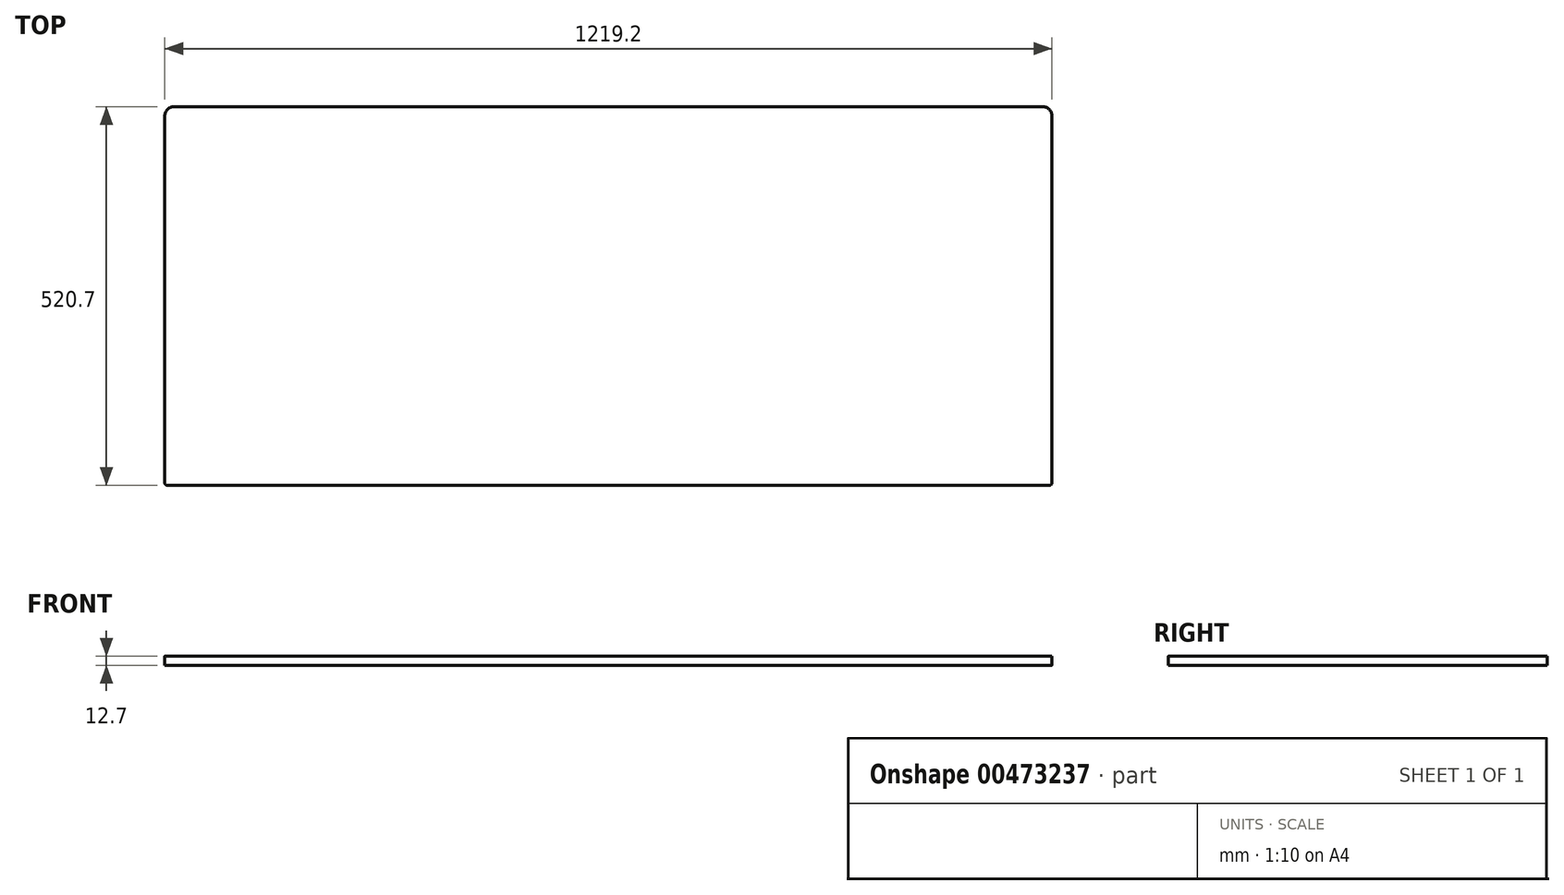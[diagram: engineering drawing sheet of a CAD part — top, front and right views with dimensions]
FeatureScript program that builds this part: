
annotation { "Feature Type Name" : "Feature", "Feature Type Description" : "" }
export const myFeature = defineFeature(function(context is Context, id is Id, definition is map)
    precondition{}
    {
        {
            var Q0;
            Q0=qCreatedBy(makeId("Top.planeOp"),FACE);
            var sketch = newSketch(context, id + "F0", { "sketchPlane" : qUnion([Q0])});
            skLineSegment(sketch, "E0.bottom", {"start": v(609.6, 260.35) * mm, "end": v(-609.6, 260.35) * mm});
            skLineSegment(sketch, "E0.top", {"start": v(609.6, -260.35) * mm, "end": v(-609.6, -260.35) * mm});
            skLineSegment(sketch, "E0.left", {"start": v(609.6, 260.35) * mm, "end": v(609.6, -260.35) * mm});
            skLineSegment(sketch, "E0.right", {"start": v(-609.6, 260.35) * mm, "end": v(-609.6, -260.35) * mm});
            skPoint(sketch, "E0.middle", {"position": v(0, 0) * mm});
            skSolve(sketch);
        }
        {
            var Q0;
            Q0=makeQuery(id+"F0.imprint","IMPRINT",FACE,{"disambiguationData":[TD([[makeQuery(id+"F0.imprint","IMPRINT",EDGE,{"derivedFrom":sQuery(id+"F0.wireOp",EDGE,"E0.bottom")}),1.0]])]});
            extrude(context, id + "F1", {"entities" : qUnion([Q0]), "depth" : 12.7 * mm});
        }
        {
            var Q0;
            Q0=makeQuery(id+"F1.opExtrude","SWEPT_EDGE",EDGE,{"disambiguationData":[OSD([sQuery(id+"F0.wireOp",EDGE,"E0.top"),sQuery(id+"F0.wireOp",EDGE,"E0.left")])]});
            var Q1;
            Q1=makeQuery(id+"F1.opExtrude","SWEPT_EDGE",EDGE,{"disambiguationData":[OSD([sQuery(id+"F0.wireOp",EDGE,"E0.top"),sQuery(id+"F0.wireOp",EDGE,"E0.right")])]});
            fillet(context, id + "F2", {"entities" : qUnion([Q0, Q1]), "radius" : 3.17 * mm, "tangentPropagation" : true, "allowEdgeOverflow" : false});
        }
        {
            var Q0;
            Q0=makeQuery(id+"F1.opExtrude","SWEPT_EDGE",EDGE,{"disambiguationData":[OSD([sQuery(id+"F0.wireOp",EDGE,"E0.bottom"),sQuery(id+"F0.wireOp",EDGE,"E0.right")])]});
            var Q1;
            Q1=makeQuery(id+"F1.opExtrude","SWEPT_EDGE",EDGE,{"disambiguationData":[OSD([sQuery(id+"F0.wireOp",EDGE,"E0.bottom"),sQuery(id+"F0.wireOp",EDGE,"E0.left")])]});
            fillet(context, id + "F3", {"entities" : qUnion([Q0, Q1]), "radius" : 12.7 * mm, "tangentPropagation" : true, "allowEdgeOverflow" : false});
        }
    });
